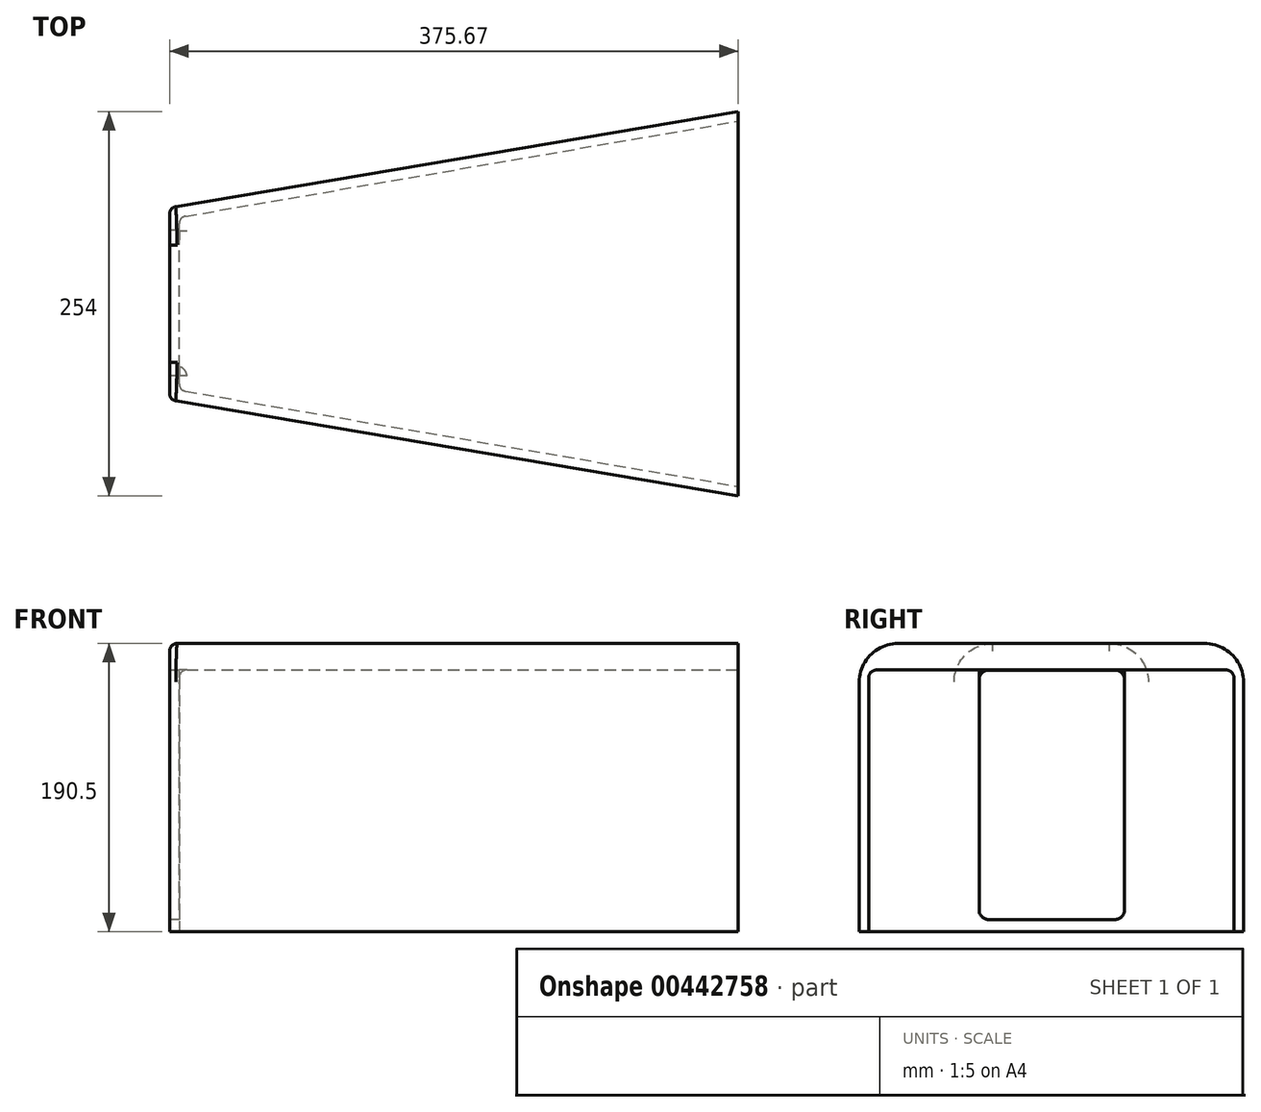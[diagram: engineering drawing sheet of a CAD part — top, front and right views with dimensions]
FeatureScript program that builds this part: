
annotation { "Feature Type Name" : "Feature", "Feature Type Description" : "" }
export const myFeature = defineFeature(function(context is Context, id is Id, definition is map)
    precondition{}
    {
        {
            var Q0;
            Q0=qCreatedBy(makeId("Top.planeOp"),FACE);
            var sketch = newSketch(context, id + "F0", { "sketchPlane" : qUnion([Q0])});
            skLineSegment(sketch, "E0", {"start": v(0, 127) * mm, "end": v(0, -127) * mm});
            skLineSegment(sketch, "E1", {"start": v(0, 0) * mm, "end": v(-375.67, 0) * mm});
            skLineSegment(sketch, "E2", {"start": v(-375.67, 63.5) * mm, "end": v(-375.67, -63.5) * mm});
            skLineSegment(sketch, "E3", {"start": v(-375.67, 63.5) * mm, "end": v(0, 127) * mm});
            skLineSegment(sketch, "E4", {"start": v(-375.67, -63.5) * mm, "end": v(0, -127) * mm});
            skSolve(sketch);
        }
        {
            var Q0;
            Q0 = qSketchRegion(id + "F0", true);
            extrude(context, id + "F1", {"entities" : qUnion([Q0]), "depth" : 190.5 * mm});
        }
        {
            var Q0;
            Q0=makeQuery(id+"F1.opExtrude","CAP_EDGE",EDGE,{"disambiguationData":[OSD([sQuery(id+"F0.wireOp",EDGE,"E3")])],"isStart":false});
            var Q1;
            Q1=makeQuery(id+"F1.opExtrude","CAP_EDGE",EDGE,{"disambiguationData":[OSD([sQuery(id+"F0.wireOp",EDGE,"E4")])],"isStart":false});
            fillet(context, id + "F2", {"entities" : qUnion([Q0, Q1]), "radius" : 25.4 * mm, "tangentPropagation" : true, "allowEdgeOverflow" : false});
        }
        {
            var Q0;
            Q0=makeQuery(id+"F1.opExtrude","CAP_EDGE",EDGE,{"disambiguationData":[OSD([sQuery(id+"F0.wireOp",EDGE,"E2")])],"isStart":false});
            fillet(context, id + "F3", {"entities" : qUnion([Q0]), "radius" : 5.08 * mm, "tangentPropagation" : true, "allowEdgeOverflow" : false});
        }
        {
            var Q0;
            Q0=qCreatedBy(makeId("Top.planeOp"),FACE);
            var sketch = newSketch(context, id + "F4", { "sketchPlane" : qUnion([Q0])});
            skLineSegment(sketch, "E5", {"start": v(0, 120.65) * mm, "end": v(0, -120.65) * mm});
            skLineSegment(sketch, "E6", {"start": v(-369.32, 0) * mm, "end": v(-369.32, 57.15) * mm});
            skLineSegment(sketch, "E7", {"start": v(-369.32, 0) * mm, "end": v(-369.32, -57.15) * mm});
            skLineSegment(sketch, "E8", {"start": v(-369.32, 57.15) * mm, "end": v(0, 120.65) * mm});
            skLineSegment(sketch, "E9", {"start": v(-369.32, -57.15) * mm, "end": v(0, -120.65) * mm});
            skSolve(sketch);
        }
        {
            var Q0;
            Q0=makeQuery(id+"F1.opExtrude","SWEPT_FACE",FACE,{"disambiguationData":[OSD([sQuery(id+"F0.wireOp",EDGE,"E2")])]});
            var sketch = newSketch(context, id + "F5", { "sketchPlane" : qUnion([Q0])});
            skLineSegment(sketch, "E10", {"start": v(-42.1, 172.9) * mm, "end": v(41.38, 172.9) * mm});
            skLineSegment(sketch, "E11", {"start": v(47.73, 166.54) * mm, "end": v(47.73, 14.39) * mm});
            skLineSegment(sketch, "E12", {"start": v(41.38, 8.04) * mm, "end": v(-42.1, 8.04) * mm});
            skLineSegment(sketch, "E13", {"start": v(-48.45, 14.39) * mm, "end": v(-48.45, 166.54) * mm});
            skPoint(sketch, "E14.visualSharp", {"position": v(-48.45, 172.9) * mm});
            skArc(sketch, "E14.filletArc", {"start": v(-42.1, 172.9) * mm, "mid": v(-46.6, 171.03) * mm, "end": v(-48.45, 166.54) * mm});
            skPoint(sketch, "E15.visualSharp", {"position": v(47.73, 172.9) * mm});
            skArc(sketch, "E15.filletArc", {"start": v(47.73, 166.54) * mm, "mid": v(45.87, 171.03) * mm, "end": v(41.38, 172.9) * mm});
            skPoint(sketch, "E16.visualSharp", {"position": v(47.73, 8.04) * mm});
            skArc(sketch, "E16.filletArc", {"start": v(41.38, 8.04) * mm, "mid": v(45.87, 9.9) * mm, "end": v(47.73, 14.39) * mm});
            skPoint(sketch, "E17.visualSharp", {"position": v(-48.45, 8.04) * mm});
            skArc(sketch, "E17.filletArc", {"start": v(-48.45, 14.39) * mm, "mid": v(-46.6, 9.9) * mm, "end": v(-42.1, 8.04) * mm});
            skSolve(sketch);
        }
        {
            var Q0;
            Q0=makeQuery(id+"F4.imprint","IMPRINT",FACE,{"disambiguationData":[TD([[makeQuery(id+"F4.imprint","IMPRINT",EDGE,{"derivedFrom":sQuery(id+"F4.wireOp",EDGE,"E5")}),-1.0]])]});
            extrude(context, id + "F6", {"entities" : qUnion([Q0]), "operationType" : NewBodyOperationType.REMOVE, "depth" : 172.97 * mm, "offsetDistance" : 25.4 * mm});
        }
        {
            var Q0;
            Q0=makeQuery(id+"F6.boolean.opBoolean","COPY",EDGE,{"derivedFrom":makeQuery(id+"F6.opExtrude","CAP_EDGE",EDGE,{"disambiguationData":[OSD([sQuery(id+"F4.wireOp",EDGE,"E9")])],"isStart":false})});
            var Q1;
            Q1=makeQuery(id+"F6.boolean.opBoolean","COPY",EDGE,{"derivedFrom":makeQuery(id+"F6.opExtrude","CAP_EDGE",EDGE,{"disambiguationData":[OSD([sQuery(id+"F4.wireOp",EDGE,"E8")])],"isStart":false})});
            fillet(context, id + "F7", {"entities" : qUnion([Q0, Q1]), "radius" : 5.08 * mm, "tangentPropagation" : true, "allowEdgeOverflow" : false});
        }
        {
            var Q0;
            Q0=makeQuery(id+"F5.imprint","IMPRINT",FACE,{"disambiguationData":[TD([[makeQuery(id+"F5.imprint","IMPRINT",EDGE,{"derivedFrom":sQuery(id+"F5.wireOp",EDGE,"E10")}),-1.0]])]});
            extrude(context, id + "F8", {"entities" : qUnion([Q0]), "operationType" : NewBodyOperationType.REMOVE, "oppositeDirection" : true, "depth" : 25.4 * mm, "offsetDistance" : 25.4 * mm});
        }
        {
            var Q0;
            Q0=makeQuery(id+"F6.boolean.opBoolean","COPY",EDGE,{"derivedFrom":makeQuery(id+"F6.opExtrude","CAP_EDGE",EDGE,{"disambiguationData":[OSD([sQuery(id+"F4.wireOp",EDGE,"E6"),sQuery(id+"F4.wireOp",EDGE,"E7")])],"isStart":false})});
            fillet(context, id + "F9", {"entities" : qUnion([Q0]), "radius" : 5.08 * mm, "tangentPropagation" : true, "allowEdgeOverflow" : false});
        }
    });
